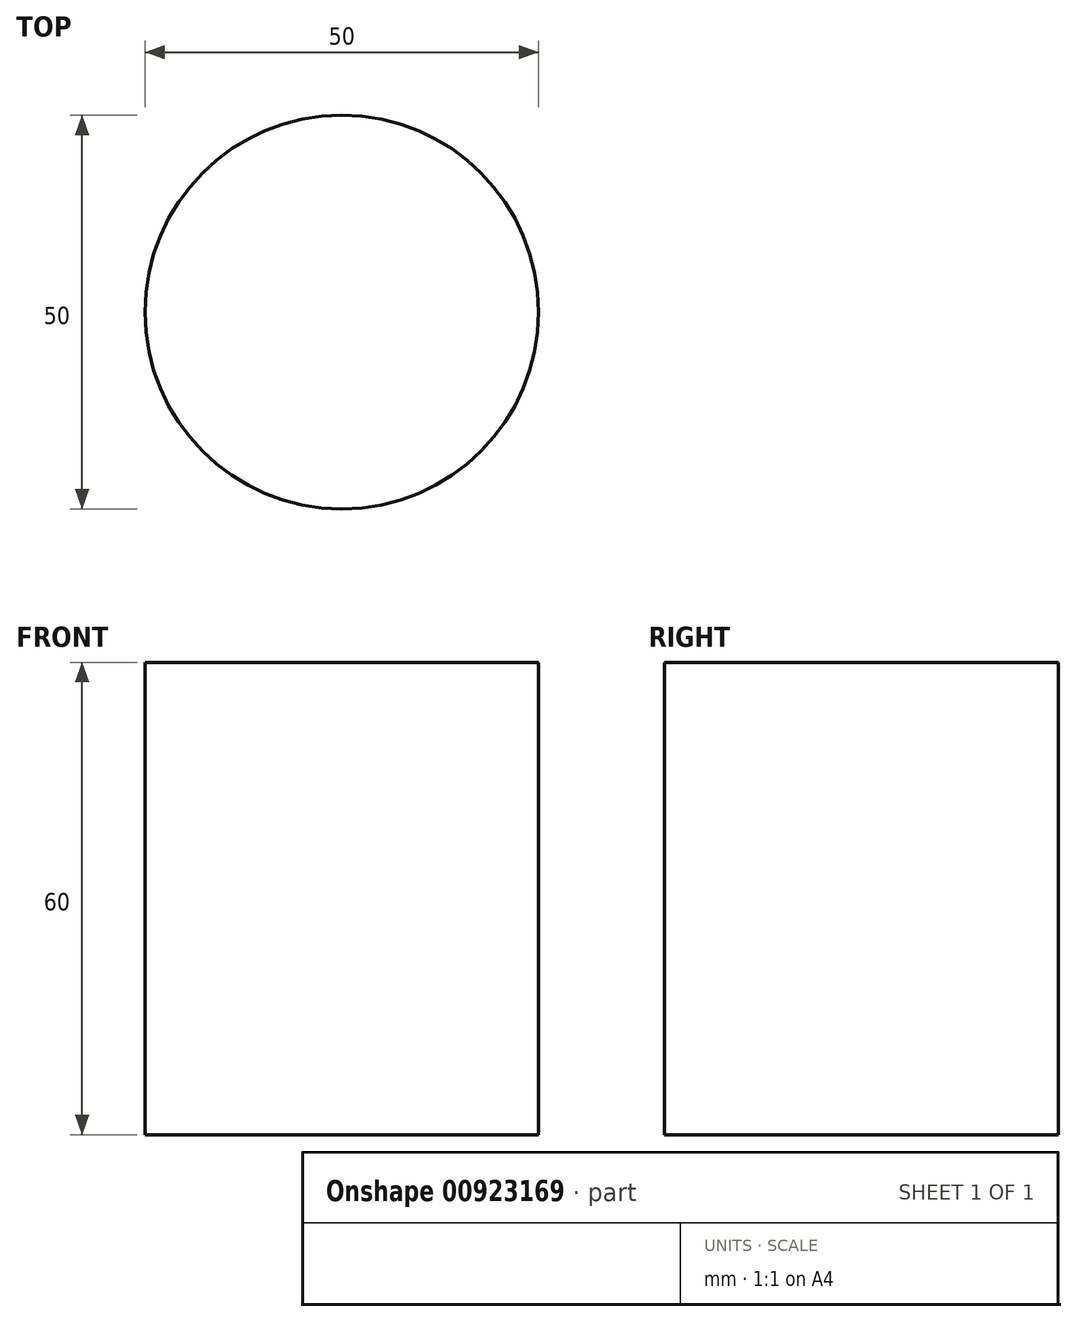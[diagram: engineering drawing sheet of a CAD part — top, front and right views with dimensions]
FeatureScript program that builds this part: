
annotation { "Feature Type Name" : "Feature", "Feature Type Description" : "" }
export const myFeature = defineFeature(function(context is Context, id is Id, definition is map)
    precondition{}
    {
        {
            var Q0;
            Q0=qCreatedBy(makeId("Top.planeOp"),FACE);
            var sketch = newSketch(context, id + "F0", { "sketchPlane" : qUnion([Q0])});
            skCircle(sketch, "E0", {"center": v(0, 0) * mm, "radius": 25 * mm});
            skSolve(sketch);
        }
        {
            var Q0;
            Q0 = qSketchRegion(id + "F0", true);
            extrude(context, id + "F1", {"entities" : qUnion([Q0]), "depth" : 60 * mm, "offsetDistance" : 25 * mm});
        }
    });
